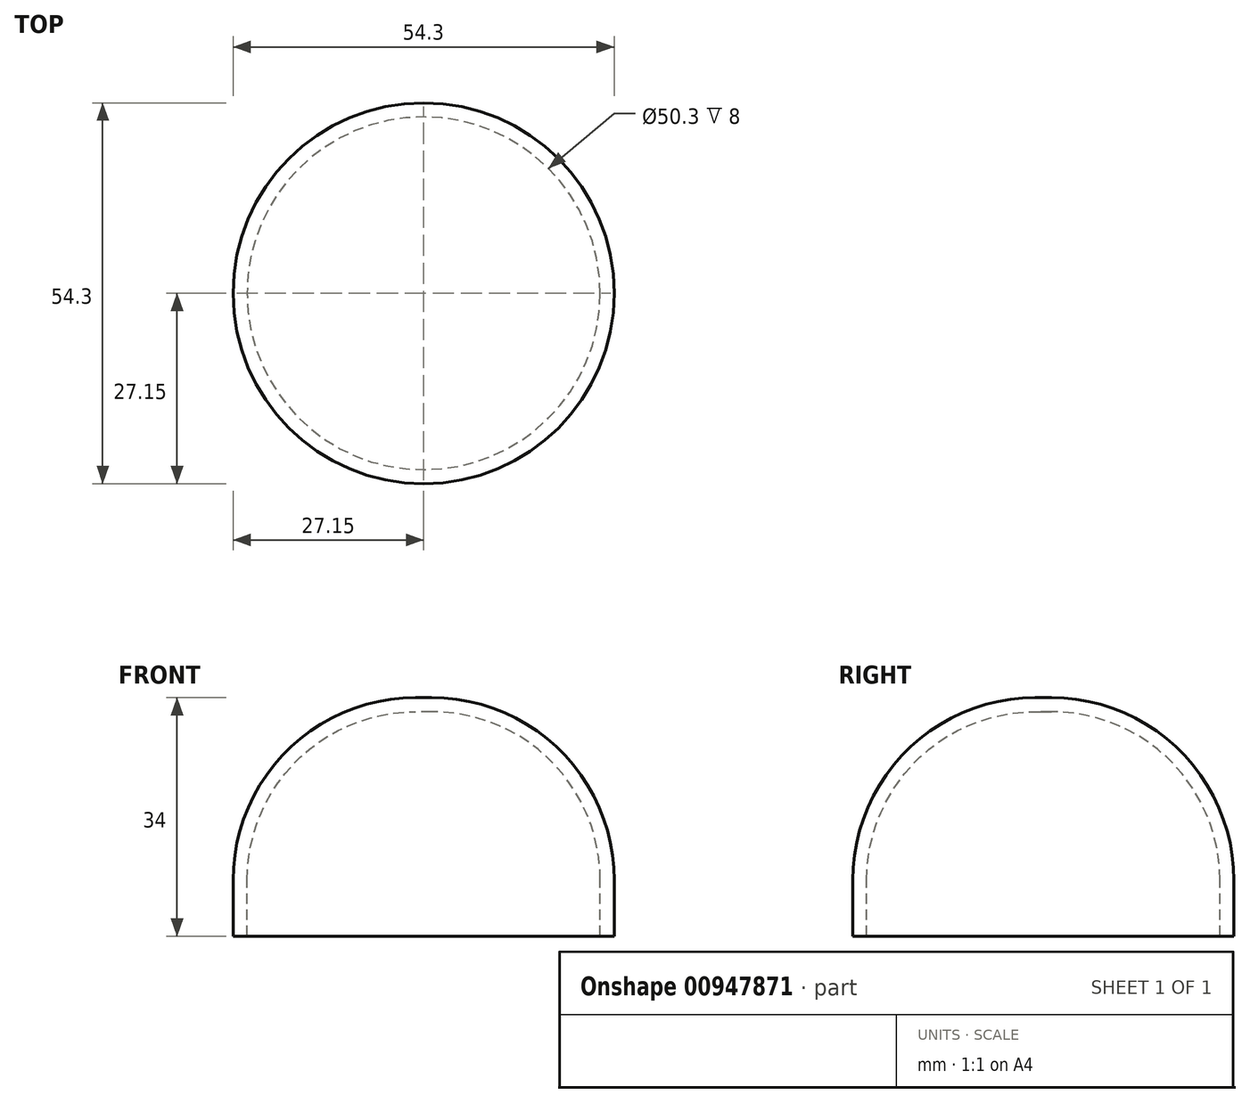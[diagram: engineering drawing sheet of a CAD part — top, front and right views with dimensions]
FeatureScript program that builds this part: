
annotation { "Feature Type Name" : "Feature", "Feature Type Description" : "" }
export const myFeature = defineFeature(function(context is Context, id is Id, definition is map)
    precondition{}
    {
        {
            var Q0;
            Q0=qCreatedBy(makeId("Top.planeOp"),FACE);
            var sketch = newSketch(context, id + "F0", { "sketchPlane" : qUnion([Q0])});
            skCircle(sketch, "E0", {"center": v(0, 0) * mm, "radius": 27.15 * mm});
            skSolve(sketch);
        }
        {
            var Q0;
            Q0 = qSketchRegion(id + "F0", true);
            extrude(context, id + "F1", {"entities" : qUnion([Q0]), "flatOperationType" : FlatOperationType.REMOVE, "depth" : 26 * mm, "offsetDistance" : 25 * mm, "domain" : OperationDomain.MODEL});
        }
        {
            var Q0;
            Q0=makeQuery(id+"F1.opExtrude","CAP_EDGE",EDGE,{"disambiguationData":[OSD([sQuery(id+"F0.wireOp",EDGE,"E0")])],"isStart":false});
            fillet(context, id + "F2", {"entities" : qUnion([Q0]), "radius" : 26 * mm, "allowEdgeOverflow" : false});
        }
        {
            var Q0;
            Q0=makeQuery(id+"F1.opExtrude","CAP_FACE",FACE,{"disambiguationData":[OSD([sQuery(id+"F0.wireOp",EDGE,"E0")])],"isStart":true});
            shell(context, id + "F3", {"entities" : qUnion([Q0]), "thickness" : 2 * mm});
        }
        {
            var Q0;
            Q0=makeQuery(id+"F1.opExtrude","CAP_FACE",FACE,{"disambiguationData":[OSD([sQuery(id+"F0.wireOp",EDGE,"E0")])],"isStart":true});
            extrude(context, id + "F4", {"entities" : qUnion([Q0]), "operationType" : NewBodyOperationType.ADD, "depth" : 8 * mm, "offsetDistance" : 25 * mm});
        }
    });
